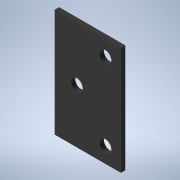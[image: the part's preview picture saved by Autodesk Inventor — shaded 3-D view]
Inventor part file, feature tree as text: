
AUTODESK INVENTOR PART (.ipt)
format: ipt  version: 2020 (Build 240168000, 168)  size: 104,960 bytes
history: native  units: mm
features: extrude x1, sketch x1
ambient origin geometry x8: Origin, YZ Plane, XZ Plane, XY Plane, X Axis, Y Axis, Z Axis, Center Point
bodies: Solid1 (feature_tree)
feature tree (2):
  extrude  "Extrusion1"  Depth=49.0mm
  sketch  "Sketch1"  dims[d0=30.0mm d1=49.0mm d2=5.5mm d3=7.0mm d4=7.0mm d5=5.5mm d6=24.5mm d7=10.0mm d8=2.0mm d9=0.0mm]
